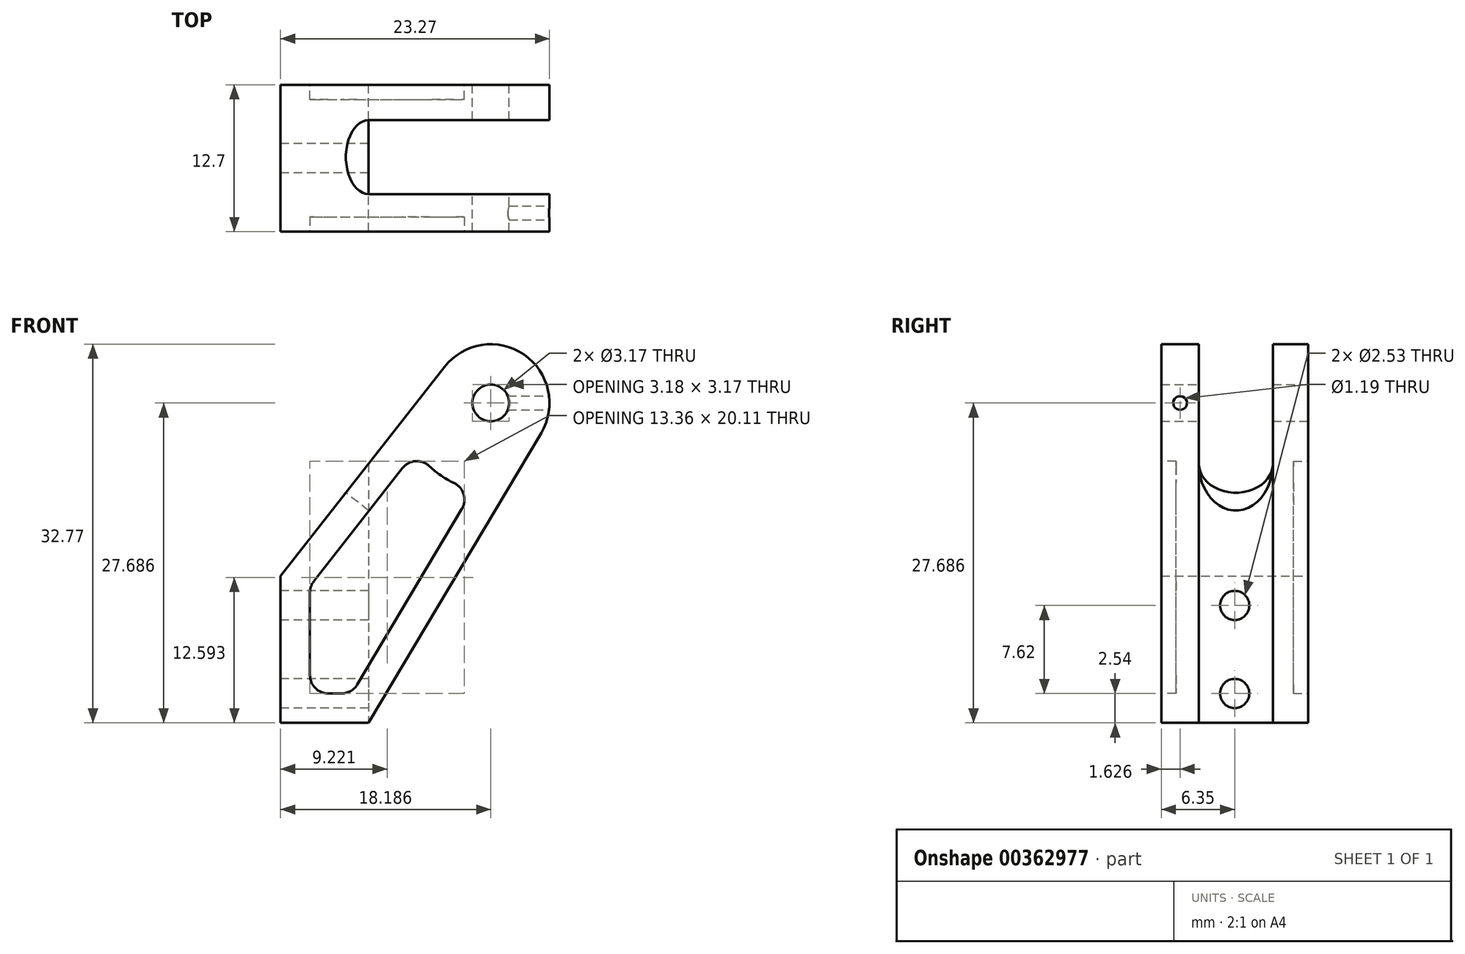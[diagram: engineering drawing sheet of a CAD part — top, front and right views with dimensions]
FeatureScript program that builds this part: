
annotation { "Feature Type Name" : "Feature", "Feature Type Description" : "" }
export const myFeature = defineFeature(function(context is Context, id is Id, definition is map)
    precondition{}
    {
        {
            var Q0;
            Q0=qCreatedBy(makeId("Front.planeOp"),FACE);
            var sketch = newSketch(context, id + "F0", { "sketchPlane" : qUnion([Q0])});
            skLineSegment(sketch, "E0", {"start": v(0, 0) * mm, "end": v(0, 12.7) * mm});
            skLineSegment(sketch, "E1", {"start": v(0, 0) * mm, "end": v(7.62, 0) * mm});
            skCircle(sketch, "E2", {"center": v(18.19, 27.69) * mm, "radius": 1.59 * mm});
            skArc(sketch, "E3", {"start": v(22.55, 25.09) * mm, "mid": v(21.06, 31.88) * mm, "end": v(14.19, 30.82) * mm});
            skLineSegment(sketch, "E4", {"start": v(0, 12.7) * mm, "end": v(14.19, 30.82) * mm});
            skLineSegment(sketch, "E5", {"start": v(7.62, 0) * mm, "end": v(22.55, 25.09) * mm});
            skSolve(sketch);
        }
        {
            var Q0;
            Q0=makeQuery(id+"F0.imprint","IMPRINT",FACE,{"disambiguationData":[TD([[makeQuery(id+"F0.imprint","IMPRINT",EDGE,{"derivedFrom":sQuery(id+"F0.wireOp",EDGE,"E0")}),-1.0]])]});
            extrude(context, id + "F1", {"entities" : qUnion([Q0]), "depth" : 12.7 * mm});
        }
        {
            var Q0;
            Q0=makeQuery(id+"F1.opExtrude","CAP_FACE",FACE,{"disambiguationData":[OSD([sQuery(id+"F0.wireOp",EDGE,"E0"),sQuery(id+"F0.wireOp",EDGE,"E1"),sQuery(id+"F0.wireOp",EDGE,"E2"),sQuery(id+"F0.wireOp",EDGE,"E3"),sQuery(id+"F0.wireOp",EDGE,"E4"),sQuery(id+"F0.wireOp",EDGE,"E5")])],"isStart":false});
            var sketch = newSketch(context, id + "F2", { "sketchPlane" : qUnion([Q0])});
            skPoint(sketch, "E6.0.end.orphan", {"position": v(14.19, 30.82) * mm});
            skPoint(sketch, "E6.0.start.orphan", {"position": v(0, 12.7) * mm});
            skPoint(sketch, "E7.0.end.orphan", {"position": v(22.55, 25.09) * mm});
            skPoint(sketch, "E7.0.start.orphan", {"position": v(7.62, 0) * mm});
            skArc(sketch, "E8", {"start": v(14.19, 30.82) * mm, "mid": v(15.32, 23.5) * mm, "end": v(22.55, 25.09) * mm});
            skLineSegment(sketch, "E9.0", {"start": v(0, 12.7) * mm, "end": v(14.19, 30.82) * mm});
            skLineSegment(sketch, "E10.0", {"start": v(0, 0) * mm, "end": v(0, 12.7) * mm});
            skLineSegment(sketch, "E11.0", {"start": v(0, 0) * mm, "end": v(7.62, 0) * mm});
            skLineSegment(sketch, "E12.0", {"start": v(7.62, 0) * mm, "end": v(22.55, 25.09) * mm});
            skLineSegment(sketch, "E13.0", {"start": v(6.64, 3.32) * mm, "end": v(15.69, 18.52) * mm});
            skArc(sketch, "E13.1", {"start": v(12.9, 22.2) * mm, "mid": v(13.88, 21.4) * mm, "end": v(14.99, 20.77) * mm});
            skLineSegment(sketch, "E13.2", {"start": v(4.13, 2.54) * mm, "end": v(5.27, 2.54) * mm});
            skLineSegment(sketch, "E13.3", {"start": v(2.54, 4.13) * mm, "end": v(2.54, 11.28) * mm});
            skLineSegment(sketch, "E13.4", {"start": v(2.88, 12.26) * mm, "end": v(10.54, 22.04) * mm});
            skPoint(sketch, "E14.visualSharp", {"position": v(11.76, 23.6) * mm});
            skArc(sketch, "E14.filletArc", {"start": v(12.9, 22.2) * mm, "mid": v(11.68, 22.65) * mm, "end": v(10.54, 22.04) * mm});
            skPoint(sketch, "E15.visualSharp", {"position": v(16.7, 20.21) * mm});
            skArc(sketch, "E15.filletArc", {"start": v(15.69, 18.52) * mm, "mid": v(15.84, 19.8) * mm, "end": v(14.99, 20.77) * mm});
            skPoint(sketch, "E16.visualSharp", {"position": v(2.54, 11.82) * mm});
            skArc(sketch, "E16.filletArc", {"start": v(2.88, 12.26) * mm, "mid": v(2.63, 11.8) * mm, "end": v(2.54, 11.28) * mm});
            skPoint(sketch, "E17.visualSharp", {"position": v(6.18, 2.54) * mm});
            skArc(sketch, "E17.filletArc", {"start": v(5.27, 2.54) * mm, "mid": v(6.06, 2.75) * mm, "end": v(6.64, 3.32) * mm});
            skPoint(sketch, "E18.visualSharp", {"position": v(2.54, 2.54) * mm});
            skArc(sketch, "E18.filletArc", {"start": v(2.54, 4.13) * mm, "mid": v(3, 3) * mm, "end": v(4.13, 2.54) * mm});
            skSolve(sketch);
        }
        {
            var Q0;
            Q0=makeQuery(id+"F2.imprint","IMPRINT",FACE,{"disambiguationData":[TD([[makeQuery(id+"F2.imprint","IMPRINT",EDGE,{"derivedFrom":sQuery(id+"F2.wireOp",EDGE,"E13.0")}),1.0]])]});
            extrude(context, id + "F3", {"entities" : qUnion([Q0]), "operationType" : NewBodyOperationType.REMOVE, "oppositeDirection" : true, "depth" : 1.27 * mm});
        }
        {
            var Q0;
            Q0=makeQuery(id+"F1.opExtrude","CAP_FACE",FACE,{"disambiguationData":[OSD([sQuery(id+"F0.wireOp",EDGE,"E0"),sQuery(id+"F0.wireOp",EDGE,"E1"),sQuery(id+"F0.wireOp",EDGE,"E2"),sQuery(id+"F0.wireOp",EDGE,"E3"),sQuery(id+"F0.wireOp",EDGE,"E4"),sQuery(id+"F0.wireOp",EDGE,"E5")])],"isStart":true});
            var sketch = newSketch(context, id + "F4", { "sketchPlane" : qUnion([Q0])});
            skLineSegment(sketch, "E19.0", {"start": v(-2.88, 12.26) * mm, "end": v(-10.54, 22.04) * mm});
            skArc(sketch, "E20.0", {"start": v(-12.9, 22.2) * mm, "mid": v(-11.68, 22.65) * mm, "end": v(-10.54, 22.04) * mm});
            skArc(sketch, "E21.0", {"start": v(-12.9, 22.2) * mm, "mid": v(-13.88, 21.4) * mm, "end": v(-14.99, 20.77) * mm});
            skArc(sketch, "E22.0", {"start": v(-15.69, 18.52) * mm, "mid": v(-15.84, 19.8) * mm, "end": v(-14.99, 20.77) * mm});
            skLineSegment(sketch, "E23.0", {"start": v(-6.64, 3.32) * mm, "end": v(-15.69, 18.52) * mm});
            skLineSegment(sketch, "E24.0", {"start": v(-2.54, 4.13) * mm, "end": v(-2.54, 11.28) * mm});
            skArc(sketch, "E25.0", {"start": v(-2.54, 4.13) * mm, "mid": v(-3, 3) * mm, "end": v(-4.13, 2.54) * mm});
            skPoint(sketch, "E26.0", {"position": v(-4.7, 2.54) * mm});
            skArc(sketch, "E27.0", {"start": v(-5.27, 2.54) * mm, "mid": v(-6.06, 2.75) * mm, "end": v(-6.64, 3.32) * mm});
            skLineSegment(sketch, "E28.0", {"start": v(-4.13, 2.54) * mm, "end": v(-5.27, 2.54) * mm});
            skArc(sketch, "E29.0", {"start": v(-2.88, 12.26) * mm, "mid": v(-2.63, 11.8) * mm, "end": v(-2.54, 11.28) * mm});
            skSolve(sketch);
        }
        {
            var Q0;
            Q0=makeQuery(id+"F4.imprint","IMPRINT",FACE,{"disambiguationData":[TD([[makeQuery(id+"F4.imprint","IMPRINT",EDGE,{"derivedFrom":sQuery(id+"F4.wireOp",EDGE,"E19.0")}),1.0]])]});
            extrude(context, id + "F5", {"entities" : qUnion([Q0]), "operationType" : NewBodyOperationType.REMOVE, "oppositeDirection" : true, "depth" : 1.27 * mm});
        }
        {
            var Q0;
            Q0=makeQuery(id+"F1.opExtrude","SWEPT_FACE",FACE,{"disambiguationData":[OSD([sQuery(id+"F0.wireOp",EDGE,"E0")])]});
            var sketch = newSketch(context, id + "F6", { "sketchPlane" : qUnion([Q0])});
            skPoint(sketch, "E30", {"position": v(6.35, 2.54) * mm});
            skPoint(sketch, "E30.positionSnap0", {"position": v(6.35, 0) * mm});
            skPoint(sketch, "E31", {"position": v(6.35, 10.16) * mm});
            skSolve(sketch);
        }
        {
            var Q0;
            Q0=sQuery(id+"F6.wireOp",VERTEX,"E30");
            var Q1;
            Q1=sQuery(id+"F6.wireOp",VERTEX,"E31");
            var Q2;
            Q2=makeQuery(id+"F1.opExtrude","SWEPT_BODY",BODY,{"disambiguationData":[OSD([sQuery(id+"F0.wireOp",EDGE,"E0"),sQuery(id+"F0.wireOp",EDGE,"E1"),sQuery(id+"F0.wireOp",EDGE,"E2"),sQuery(id+"F0.wireOp",EDGE,"E3"),sQuery(id+"F0.wireOp",EDGE,"E4"),sQuery(id+"F0.wireOp",EDGE,"E5")])]});
            hole(context, id + "F7", {"style" : HoleStyle.SIMPLE, "endStyle" : HoleEndStyle.THROUGH, "standardTappedOrClearance" : lookupTablePath({ "standard" : "ANSI", "size" : "#39 (0.1)", "type" : "Drilled" }), "standardBlindInLast" : lookupTablePath({ "standard" : "ANSI", "size" : "#39", "type" : "Drilled" }), "holeDiameter" : 2.53 * mm, "tappedDepth" : 3 * mm, "tapClearance" : 3, "locations" : qUnion([Q0, Q1]), "scope" : qUnion([Q2])});
        }
        {
            var Q0;
            Q0=makeQuery(id+"F1.opExtrude","SWEPT_FACE",FACE,{"disambiguationData":[OSD([sQuery(id+"F0.wireOp",EDGE,"E1")])]});
            var sketch = newSketch(context, id + "F8", { "sketchPlane" : qUnion([Q0])});
            skLineSegment(sketch, "E32.0", {"start": v(7.62, 12.7) * mm, "end": v(7.62, 0) * mm});
            skLineSegment(sketch, "E33", {"start": v(23.27, 9.45) * mm, "end": v(23.27, 3.05) * mm});
            skLineSegment(sketch, "E34.0", {"start": v(7.62, 3.05) * mm, "end": v(23.27, 3.05) * mm});
            skLineSegment(sketch, "E35.0", {"start": v(7.62, 9.45) * mm, "end": v(23.27, 9.45) * mm});
            skPoint(sketch, "E36.0.end.orphan", {"position": v(22.55, 0) * mm});
            skSolve(sketch);
        }
        {
            var Q0;
            Q0=makeQuery(id+"F8.imprint","IMPRINT",FACE,{"disambiguationData":[TD([[makeQuery(id+"F8.imprint","IMPRINT",EDGE,{"derivedFrom":sQuery(id+"F8.wireOp",EDGE,"E33")}),-1.0]])]});
            extrude(context, id + "F9", {"entities" : qUnion([Q0]), "operationType" : NewBodyOperationType.REMOVE, "endBound" : BoundingType.THROUGH_ALL, "oppositeDirection" : true, "depth" : 25.4 * mm});
        }
        {
            var Q0;
            Q0=makeQuery(id+"F1.opExtrude","SWEPT_FACE",FACE,{"disambiguationData":[OSD([sQuery(id+"F0.wireOp",EDGE,"E4")])]});
            var sketch = newSketch(context, id + "F10", { "sketchPlane" : qUnion([Q0])});
            skCircle(sketch, "E37", {"center": v(6.25, 22.36) * mm, "radius": 3.2 * mm});
            skSolve(sketch);
        }
        {
            var Q0;
            {var subQ1=makeQuery(id+"F1.opExtrude","SWEPT_FACE",FACE,{"disambiguationData":[OSD([sQuery(id+"F0.wireOp",EDGE,"E4")])]});var subQ2=makeQuery(id+"F9.boolean.opBoolean","INTERSECT",EDGE,{"derivedFrom":[subQ1,makeQuery(id+"F9.opExtrude","SWEPT_FACE",FACE,{"disambiguationData":[OSD([sQuery(id+"F8.wireOp",EDGE,"E32.0")])]})]});Q0=makeQuery(id+"F10.imprint","IMPRINT",FACE,{"disambiguationData":[TD([[makeQuery(id+"F10.imprint","IMPRINT",EDGE,{"derivedFrom":subQ2}),-1.0]])]});}
            extrude(context, id + "F11", {"entities" : qUnion([Q0]), "operationType" : NewBodyOperationType.REMOVE, "endBound" : BoundingType.THROUGH_ALL, "oppositeDirection" : true, "depth" : 25.4 * mm});
        }
        {
            var Q0;
            Q0=qCreatedBy(makeId("Right.planeOp"),FACE);
            cPlane(context, id + "F12", {"entities" : qUnion([Q0]), "cplaneType" : CPlaneType.OFFSET, "offset" : 23.42 * mm, "width" : 152.4 * mm, "height" : 152.4 * mm});
        }
        {
            var Q0;
            Q0=qCreatedBy(id+"F12.planeOp",FACE);
            var sketch = newSketch(context, id + "F13", { "sketchPlane" : qUnion([Q0])});
            skPoint(sketch, "E38.0", {"position": v(-11.07, 0) * mm});
            skPoint(sketch, "E39", {"position": v(-11.07, 27.69) * mm});
            skCircle(sketch, "E40", {"center": v(-11.07, 27.69) * mm, "radius": 0.6 * mm});
            skSolve(sketch);
        }
        {
            var Q0;
            Q0=makeQuery(id+"F13.imprint","IMPRINT",FACE,{"disambiguationData":[TD([[makeQuery(id+"F13.imprint","IMPRINT",EDGE,{"derivedFrom":sQuery(id+"F13.wireOp",EDGE,"E40")}),1.0]])]});
            extrude(context, id + "F14", {"entities" : qUnion([Q0]), "operationType" : NewBodyOperationType.REMOVE, "oppositeDirection" : true, "depth" : 4.24 * mm});
        }
    });
